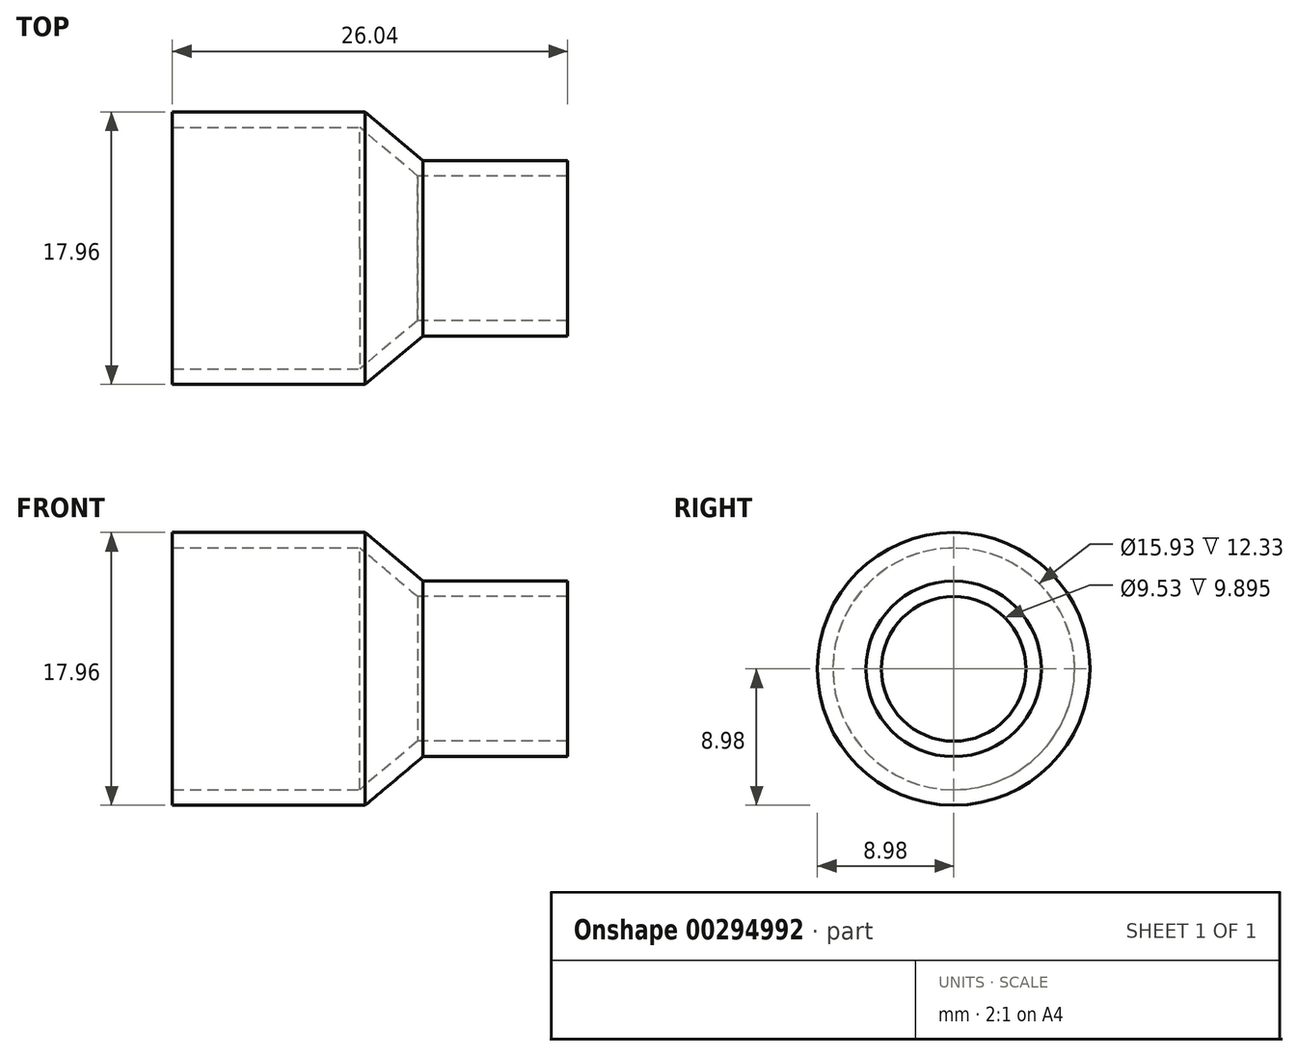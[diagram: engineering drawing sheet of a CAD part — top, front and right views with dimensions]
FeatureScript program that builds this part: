
annotation { "Feature Type Name" : "Feature", "Feature Type Description" : "" }
export const myFeature = defineFeature(function(context is Context, id is Id, definition is map)
    precondition{}
    {
        {
            var Q0;
            Q0=qCreatedBy(makeId("Right.planeOp"),FACE);
            var sketch = newSketch(context, id + "F0", { "sketchPlane" : qUnion([Q0])});
            skCircle(sketch, "E0", {"center": v(0, 0) * mm, "radius": 8.98 * mm});
            skSolve(sketch);
        }
        {
            var Q0;
            Q0 = qSketchRegion(id + "F0", true);
            extrude(context, id + "F1", {"entities" : qUnion([Q0]), "oppositeDirection" : true, "depth" : 12.7 * mm});
        }
        {
            var Q0;
            Q0=qCreatedBy(makeId("Right.planeOp"),FACE);
            cPlane(context, id + "F2", {"entities" : qUnion([Q0]), "cplaneType" : CPlaneType.OFFSET, "offset" : 3.8 * mm, "width" : 152.4 * mm, "height" : 152.4 * mm});
        }
        {
            var Q0;
            Q0=qCreatedBy(id+"F2.planeOp",FACE);
            var sketch = newSketch(context, id + "F3", { "sketchPlane" : qUnion([Q0])});
            skPoint(sketch, "E1.0", {"position": v(0, 0) * mm});
            skCircle(sketch, "E2", {"center": v(0, 0) * mm, "radius": 5.78 * mm});
            skSolve(sketch);
        }
        {
            var Q0;
            Q0 = qSketchRegion(id + "F3", true);
            extrude(context, id + "F4", {"entities" : qUnion([Q0]), "depth" : 9.52 * mm});
        }
        {
            var Q0;
            Q0=makeQuery(id+"F1.opExtrude","CAP_FACE",FACE,{"disambiguationData":[OSD([sQuery(id+"F0.wireOp",EDGE,"FSnA3JPl-jaDT-1N9C-D5yt-aIQ6gAFVFGIr"),sQuery(id+"F0.wireOp",EDGE,"E0")])],"isStart":true});
            var Q1;
            Q1=makeQuery(id+"F4.opExtrude","CAP_FACE",FACE,{"disambiguationData":[OSD([sQuery(id+"F3.wireOp",EDGE,"bssw4aSf-YQa8-k349-BioW-mXQyCm2wpGI0"),sQuery(id+"F3.wireOp",EDGE,"E2")])],"isStart":true});
            loft(context, id + "F5", {"operationType" : NewBodyOperationType.ADD, "sheetProfilesArray" : [{ "sheetProfileEntities" : qUnion([Q0]) }, { "sheetProfileEntities" : qUnion([Q1]) }]});
        }
        {
            var Q0;
            Q0=makeQuery(id+"F4.opExtrude","CAP_FACE",FACE,{"disambiguationData":[OSD([sQuery(id+"F3.wireOp",EDGE,"E2")])],"isStart":false});
            var Q1;
            Q1=makeQuery(id+"F1.opExtrude","CAP_FACE",FACE,{"disambiguationData":[OSD([sQuery(id+"F0.wireOp",EDGE,"E0")])],"isStart":false});
            shell(context, id + "F6", {"entities" : qUnion([Q0, Q1]), "thickness" : 1.02 * mm});
        }
    });
